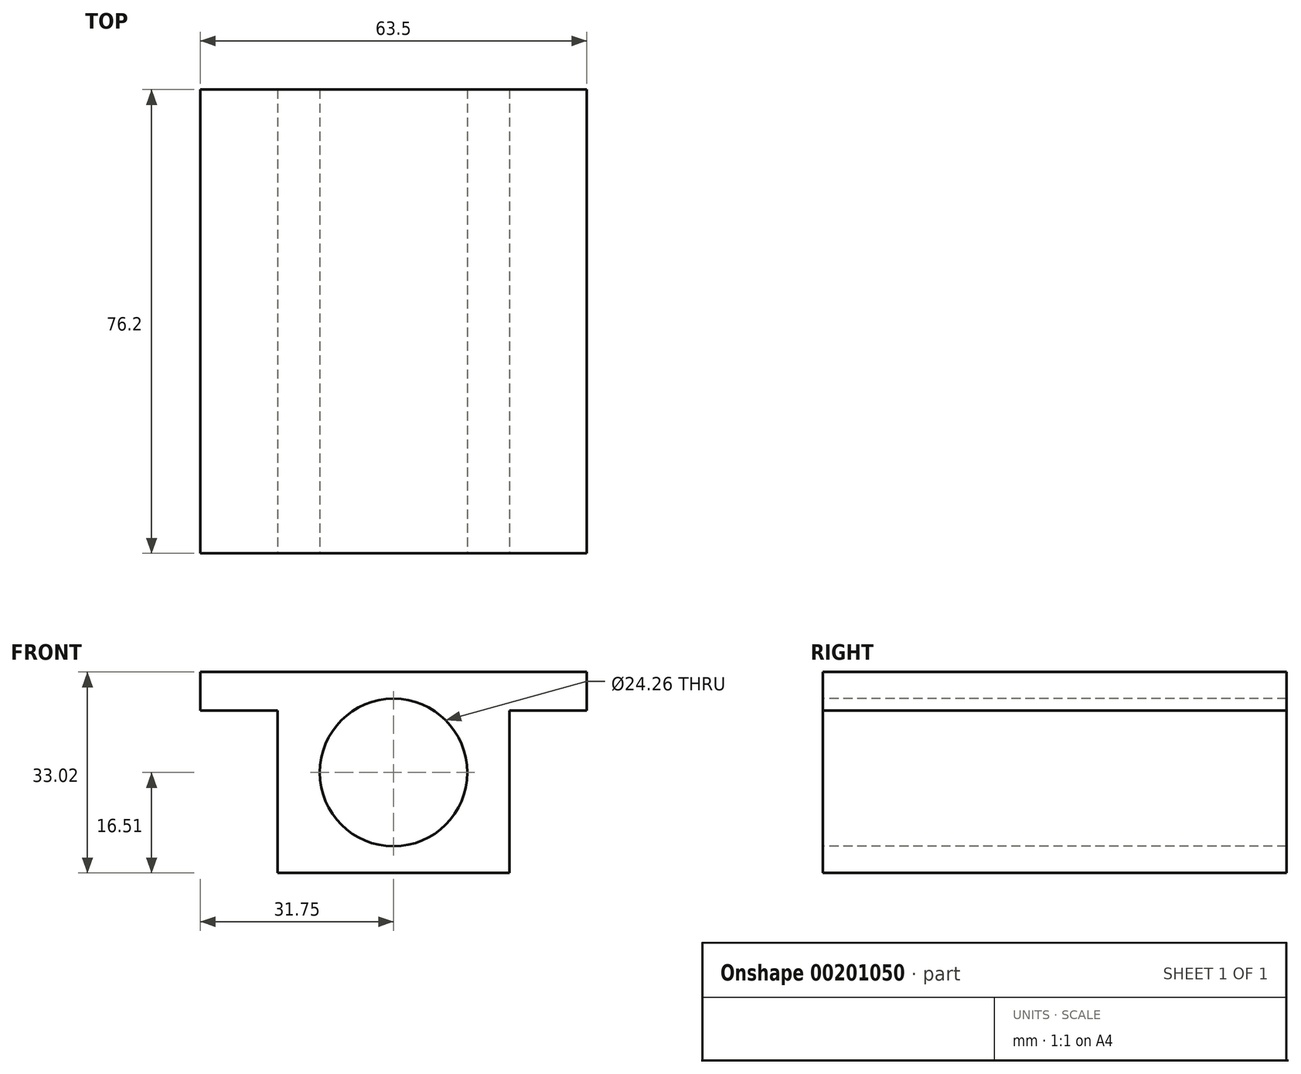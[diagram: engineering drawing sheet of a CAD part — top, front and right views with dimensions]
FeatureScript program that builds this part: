
annotation { "Feature Type Name" : "Feature", "Feature Type Description" : "" }
export const myFeature = defineFeature(function(context is Context, id is Id, definition is map)
    precondition{}
    {
        {
            var Q0;
            Q0=qCreatedBy(makeId("Top.planeOp"),FACE);
            var sketch = newSketch(context, id + "F0", { "sketchPlane" : qUnion([Q0])});
            skLineSegment(sketch, "E0.bottom", {"start": v(31.75, 38.1) * mm, "end": v(-31.75, 38.1) * mm});
            skLineSegment(sketch, "E0.top", {"start": v(31.75, -38.1) * mm, "end": v(-31.75, -38.1) * mm});
            skLineSegment(sketch, "E0.left", {"start": v(31.75, 38.1) * mm, "end": v(31.75, -38.1) * mm});
            skLineSegment(sketch, "E0.right", {"start": v(-31.75, 38.1) * mm, "end": v(-31.75, -38.1) * mm});
            skPoint(sketch, "E0.middle", {"position": v(0, 0) * mm});
            skSolve(sketch);
        }
        {
            var Q0;
            Q0 = qSketchRegion(id + "F0", true);
            var Q1;
            Q1 = qSketchRegion(id + "F4", true);
            extrude(context, id + "F1", {"entities" : qUnion([Q0, Q1]), "depth" : 33.02 * mm});
        }
        {
            var Q0;
            Q0=makeQuery(id+"F1.opExtrude","SWEPT_FACE",FACE,{"disambiguationData":[OSD([sQuery(id+"F0.wireOp",EDGE,"E0.top")])]});
            var sketch = newSketch(context, id + "F2", { "sketchPlane" : qUnion([Q0])});
            skLineSegment(sketch, "E1", {"start": v(0, 33.02) * mm, "end": v(0, 0) * mm, "construction": true});
            skLineSegment(sketch, "E2", {"start": v(-31.75, 16.51) * mm, "end": v(31.75, 16.51) * mm, "construction": true});
            skCircle(sketch, "E3", {"center": v(0, 16.51) * mm, "radius": 12.13 * mm});
            skSolve(sketch);
        }
        {
            var Q0;
            Q0 = qSketchRegion(id + "F2", true);
            extrude(context, id + "F3", {"entities" : qUnion([Q0]), "operationType" : NewBodyOperationType.REMOVE, "oppositeDirection" : true, "depth" : 100.08 * mm});
        }
        {
            var Q0;
            Q0=makeQuery(id+"F1.opExtrude","SWEPT_FACE",FACE,{"disambiguationData":[OSD([sQuery(id+"F0.wireOp",EDGE,"E0.top")])]});
            var sketch = newSketch(context, id + "F4", { "sketchPlane" : qUnion([Q0])});
            skLineSegment(sketch, "E4.bottom", {"start": v(31.75, 0) * mm, "end": v(19.05, 0) * mm});
            skLineSegment(sketch, "E4.top", {"start": v(31.75, 26.67) * mm, "end": v(19.05, 26.67) * mm});
            skLineSegment(sketch, "E4.left", {"start": v(31.75, 0) * mm, "end": v(31.75, 26.67) * mm});
            skLineSegment(sketch, "E4.right", {"start": v(19.05, 0) * mm, "end": v(19.05, 26.67) * mm});
            skLineSegment(sketch, "E5.MirrorCS", {"start": v(-19.05, 0) * mm, "end": v(-19.05, 26.67) * mm});
            skLineSegment(sketch, "E6.MirrorCS", {"start": v(-31.75, 0) * mm, "end": v(-31.75, 26.67) * mm});
            skLineSegment(sketch, "E7.MirrorCS", {"start": v(-31.75, 0) * mm, "end": v(-19.05, 0) * mm});
            skLineSegment(sketch, "E8.MirrorCS", {"start": v(-31.75, 26.67) * mm, "end": v(-19.05, 26.67) * mm});
            skSolve(sketch);
        }
        {
            var Q0;
            Q0 = qSketchRegion(id + "F4", true);
            extrude(context, id + "F5", {"entities" : qUnion([Q0]), "operationType" : NewBodyOperationType.REMOVE, "endBound" : BoundingType.THROUGH_ALL, "oppositeDirection" : true, "depth" : 25.4 * mm});
        }
    });
